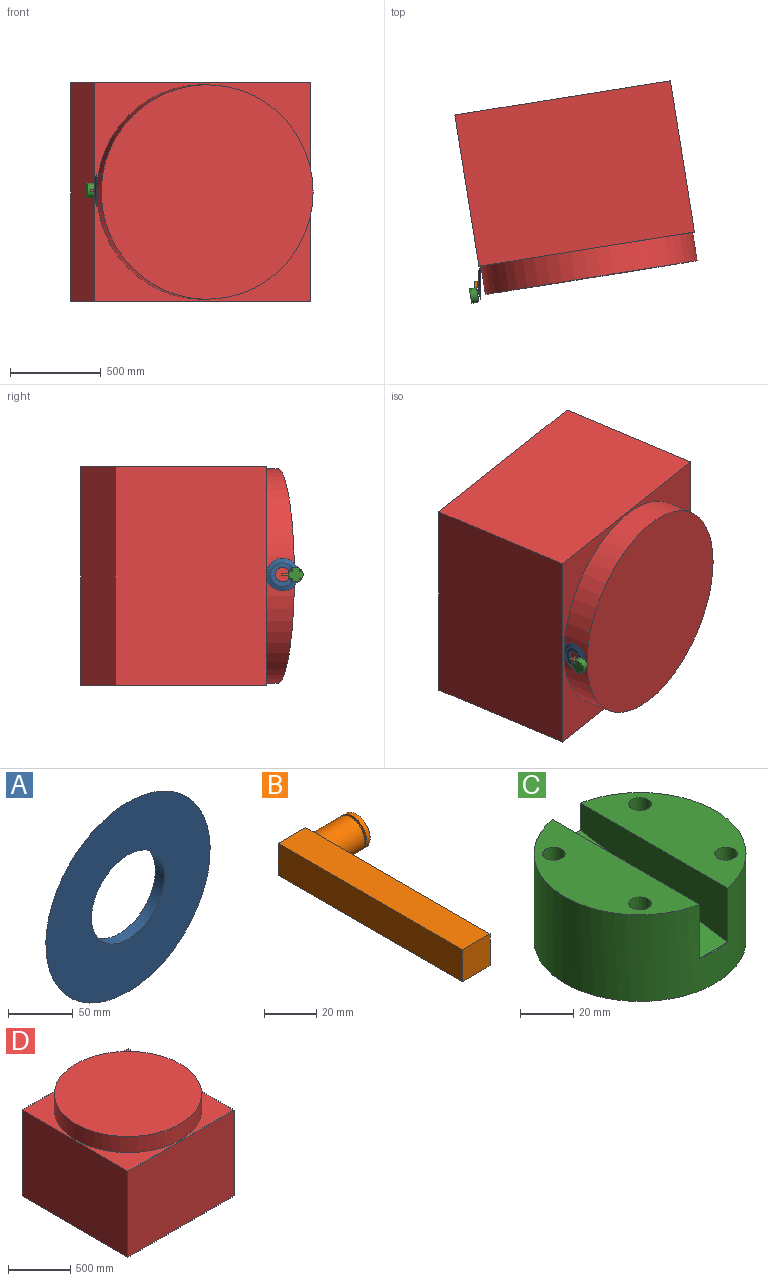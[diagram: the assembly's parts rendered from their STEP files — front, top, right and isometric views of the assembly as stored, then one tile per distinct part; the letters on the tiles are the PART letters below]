
ASSEMBLY  parts=4 mates=4
PART A: 4 faces, bbox 180x10x180 mm
  f0: plane 130.5x130.5mm, normal (0,1,0), area 8348.6mm2, adj f1,f3
  f1: cylinder r=40mm len=80mm, axis (0,-1,0), area 2513.3mm2, adj f0,f2
  f2: plane 180x180mm, normal (0,-1,0), area 20420.4mm2, adj f1,f3
  f3: cone r=90mm half-angle=68deg, axis (0,-1,0), area 13019.8mm2, adj f0,f2
PART B: 14 faces, bbox 35x100x15 mm
  f0: plane 7.5x7.5mm, normal (1,0,0), area 12.1mm2, adj f2,f6,f8
  f1: plane 92.5x15mm, normal (1,0,0), area 1299.1mm2, adj f4,f6,f7,f8
  f2: plane 15x15mm, normal (0,1,0), area 225mm2, adj f0,f3,f5,f6,f7
  f3: plane 100x15mm, normal (-1,0,0), area 1500mm2, adj f2,f4,f6,f7
  f4: plane 15x15mm, normal (0,-1,0), area 225mm2, adj f1,f3,f6,f7
  f5: plane 7.5x7.5mm, normal (1,0,0), area 12.1mm2, adj f2,f7,f8
  f6: plane 100x15mm, normal (0,0,1), area 1500mm2, adj f0,f1,f2,f3,f4
  f7: plane 100x15mm, normal (0,0,-1), area 1500mm2, adj f1,f2,f3,f4,f5
  f8: cylinder r=7.5mm len=17mm, axis (-1,0,0), area 801.1mm2, adj f0,f1,f5,f9
  f9: plane 15x15mm, normal (1,0,0), area 44mm2, adj f8,f10
  f10: cylinder r=6.5mm len=13mm, axis (-1,0,0), area 40.8mm2, adj f9,f13
  f11: cylinder r=7.5mm len=15mm, axis (-1,0,0), area 94.2mm2, adj f12,f13
  f12: plane 15x15mm, normal (1,0,0), area 176.7mm2, adj f11
  f13: plane 15x15mm, normal (-1,0,0), area 44mm2, adj f10,f11
PART C: 13 faces, bbox 80x80x40 mm
  f0: plane 15x0.71mm, normal (0,0,1), area 7.1mm2, adj f6,f11
  f1: plane 78.58x32.5mm, normal (0,0,1), area 1803.3mm2, adj f3,f4,f6,f10
  f2: cylinder r=4.25mm len=40mm, axis (0,0,-1), area 1068.1mm2, adj f7,f8
  f3: cylinder r=4.25mm len=40mm, axis (0,0,-1), area 1068.1mm2, adj f1,f8
  f4: cylinder r=4.25mm len=40mm, axis (0,0,-1), area 1068.1mm2, adj f1,f8
  f5: cylinder r=4.25mm len=40mm, axis (0,0,-1), area 1068.1mm2, adj f7,f8
  f6: cylinder r=40mm len=80mm, axis (0,0,-1), area 9487.2mm2, adj f0,f1,f7,f8,f9,f10,f12
  f7: plane 78.58x32.5mm, normal (0,0,1), area 1803.3mm2, adj f2,f5,f6,f9
  f8: plane 80x80mm, normal (0,0,-1), area 4799.6mm2, adj f2,f3,f4,f5,f6
  f9: plane 78.58x25mm, normal (1,0,0), area 1473.4mm2, adj f6,f7,f11
  f10: plane 78.58x25mm, normal (-1,0,0), area 1473.4mm2, adj f1,f6,f11
  f11: plane 78.58x15mm, normal (0,-0.16,0.99), area 1193.5mm2, adj f0,f9,f10,f12
  f12: plane 15x0.71mm, normal (0,0,1), area 7.1mm2, adj f6,f11
PART D: 8 faces, bbox 1200x1200x1000 mm
  f0: plane 1180x1180mm, normal (0,0,1), area 1093588.4mm2, adj f1
  f1: cylinder r=590mm len=1180mm, axis (0,0,1), area 583521.7mm2, adj f0,f2
  f2: plane 1200x1200mm, normal (0,0,1), area 346411.6mm2, adj f1,f3,f4,f5,f6
  f3: plane 1200x842.59mm, normal (1,0,0), area 1011111.1mm2, adj f2,f4,f5,f7
  f4: plane 1200x842.59mm, normal (0,1,0), area 1011111.1mm2, adj f2,f3,f6,f7
  f5: plane 1200x842.59mm, normal (0,-1,0), area 1011111.1mm2, adj f2,f3,f6,f7
  f6: plane 1200x842.59mm, normal (-1,0,0), area 1011111.1mm2, adj f2,f4,f5,f7
  f7: plane 1200x1200mm, normal (0,0,-1), area 1440000mm2, adj f3,f4,f5,f6
PLACE A rot(axis=(-0.58,0.58,0.58),120deg) t=(-25.91,47.95,41.44)mm
PLACE B t=(-40.91,5.45,41.44)mm fixed
PLACE C rot(axis=(-0.08,0.99,0.08),90.4deg) t=(-76.89,-25.47,41.44)mm
PLACE D rot(axis=(0.99,0.08,0.08),90.4deg) t=(429.7,1063.81,33.94)mm
MATE planar B.f6 <-> C.f9  axis (0,0,1) through (-48.41,5.45,48.94)mm
MATE planar B.f3 <-> C.f11  axis (-1,0,0) through (-55.91,5.45,41.44)mm
MATE planar A.f1 <-> B.f8  axis (1,0,0) through (-20.91,47.95,41.44)mm
MATE parallel D.f6 <-> C.f6  axis (-0.99,-0.16,0) through (-96.66,553.48,33.94)mm
